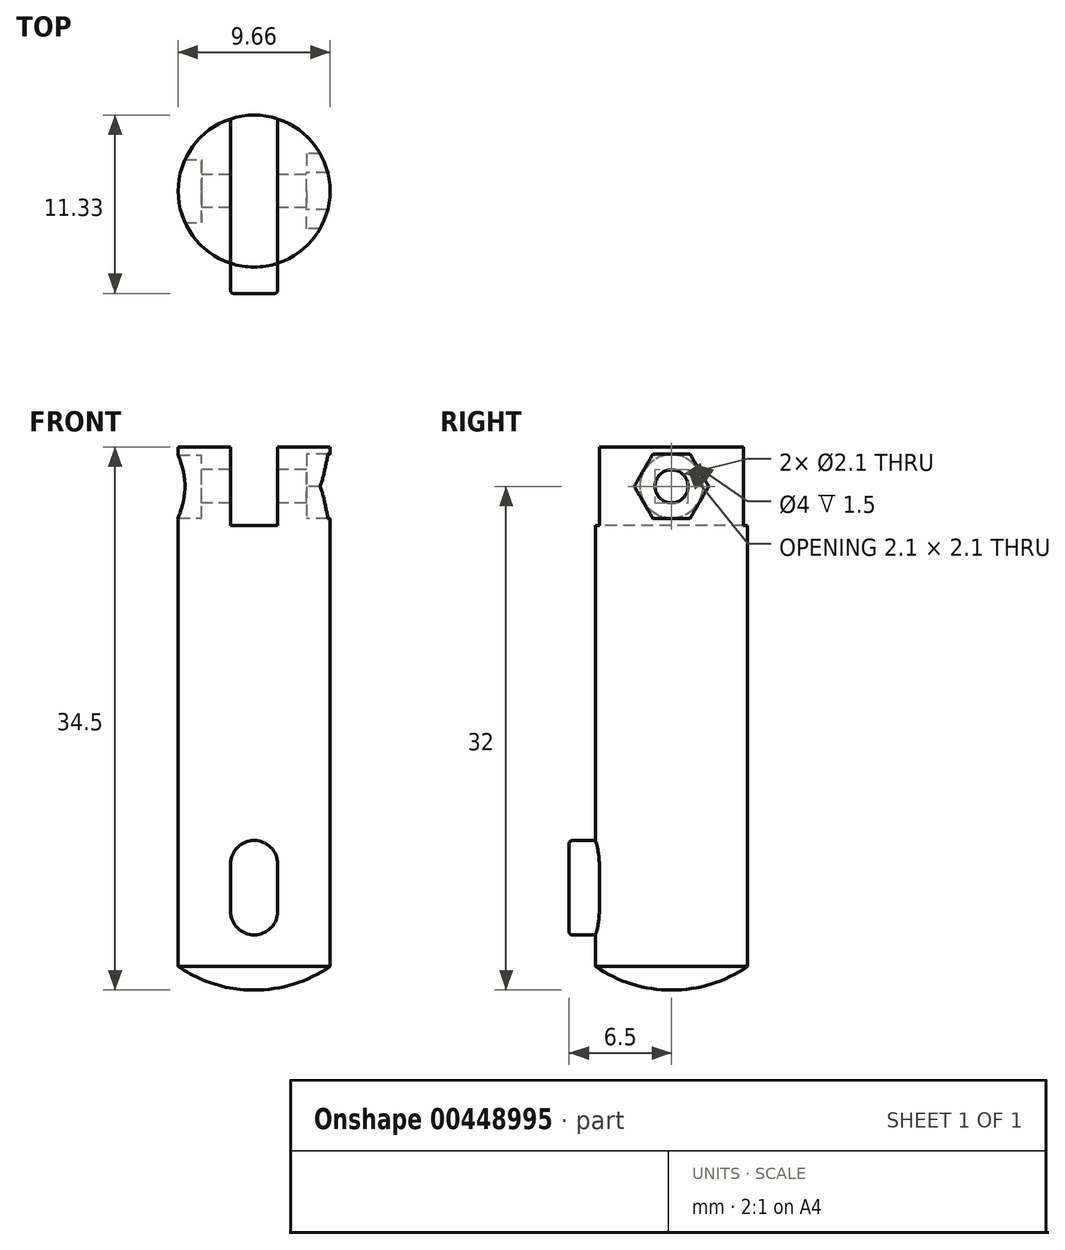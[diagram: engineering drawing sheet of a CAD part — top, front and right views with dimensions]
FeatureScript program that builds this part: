
annotation { "Feature Type Name" : "Feature", "Feature Type Description" : "" }
export const myFeature = defineFeature(function(context is Context, id is Id, definition is map)
    precondition{}
    {
        {
            var Q0;
            Q0=qCreatedBy(makeId("Top.planeOp"),FACE);
            var sketch = newSketch(context, id + "F0", { "sketchPlane" : qUnion([Q0])});
            skCircle(sketch, "E0", {"center": v(0, 0) * mm, "radius": 4.83 * mm});
            skSolve(sketch);
        }
        {
            var Q0;
            Q0 = qSketchRegion(id + "F0", true);
            extrude(context, id + "F1", {"entities" : qUnion([Q0]), "depth" : 33 * mm});
        }
        {
            var Q0;
            Q0=qCreatedBy(makeId("Front.planeOp"),FACE);
            var sketch = newSketch(context, id + "F2", { "sketchPlane" : qUnion([Q0])});
            skLineSegment(sketch, "E1", {"start": v(0, 3.5) * mm, "end": v(0, 6.5) * mm, "construction": true});
            skArc(sketch, "E2.0.startCap", {"start": v(1.5, 3.5) * mm, "mid": v(0, 2) * mm, "end": v(-1.5, 3.5) * mm});
            skArc(sketch, "E2.0.endCap", {"start": v(-1.5, 6.5) * mm, "mid": v(0, 8) * mm, "end": v(1.5, 6.5) * mm});
            skLineSegment(sketch, "E2.0.left", {"start": v(-1.5, 3.5) * mm, "end": v(-1.5, 6.5) * mm});
            skLineSegment(sketch, "E2.0.right", {"start": v(1.5, 3.5) * mm, "end": v(1.5, 6.5) * mm});
            skSolve(sketch);
        }
        {
            var Q0;
            Q0 = qSketchRegion(id + "F2", true);
            var Q1;
            Q1 = qBodyType(qCreatedBy(id + "F2" ,EDGE), BodyType.WIRE);
            extrude(context, id + "F3", {"entities" : qUnion([Q0]), "operationType" : NewBodyOperationType.ADD, "surfaceEntities" : qUnion([Q1]), "depth" : 6.5 * mm});
        }
        {
            var Q0;
            Q0=makeQuery(id+"F3.opExtrude","CAP_FACE",FACE,{"disambiguationData":[OSD([sQuery(id+"F2.wireOp",EDGE,"E2.0.startCap"),sQuery(id+"F2.wireOp",EDGE,"E2.0.endCap"),sQuery(id+"F2.wireOp",EDGE,"E2.0.left"),sQuery(id+"F2.wireOp",EDGE,"E2.0.right")])],"isStart":false});
            fillet(context, id + "F4", {"entities" : qUnion([Q0]), "radius" : 0.2 * mm, "tangentPropagation" : true, "allowEdgeOverflow" : false});
        }
        {
            var Q0;
            Q0=qCreatedBy(makeId("Front.planeOp"),FACE);
            var sketch = newSketch(context, id + "F5", { "sketchPlane" : qUnion([Q0])});
            skLineSegment(sketch, "E3", {"start": v(0, 0) * mm, "end": v(0, -2.82) * mm, "construction": true});
            skLineSegment(sketch, "E4", {"start": v(-4.62, -1.5) * mm, "end": v(4.9, -1.5) * mm, "construction": true});
            skLineSegment(sketch, "E5.0", {"start": v(-4.83, 0) * mm, "end": v(0, 0) * mm});
            skArc(sketch, "E6", {"start": v(-4.83, 0) * mm, "mid": v(-2.53, -1.12) * mm, "end": v(0, -1.5) * mm});
            skLineSegment(sketch, "E7", {"start": v(0, 0) * mm, "end": v(0, -1.5) * mm});
            skPoint(sketch, "E8.orphan", {"position": v(4.83, 0) * mm});
            skSolve(sketch);
        }
        {
            var Q0;
            Q0 = qSketchRegion(id + "F5", true);
            var Q1;
            Q1=sQuery(id+"F5.wireOp",EDGE,"E3");
            revolve(context, id + "F6", {"operationType" : NewBodyOperationType.ADD, "entities" : qUnion([Q0]), "axis" : qUnion([Q1]), "revolveType" : RevolveType.FULL});
        }
        {
            var Q0;
            Q0=makeQuery(id+"F1.opExtrude","CAP_FACE",FACE,{"disambiguationData":[OSD([sQuery(id+"F0.wireOp",EDGE,"E0")])],"isStart":false});
            var sketch = newSketch(context, id + "F7", { "sketchPlane" : qUnion([Q0])});
            skLineSegment(sketch, "E9", {"start": v(0, 11.02) * mm, "end": v(0, -10.17) * mm, "construction": true});
            skLineSegment(sketch, "E10.0", {"start": v(-1.5, 4.59) * mm, "end": v(-1.5, -4.59) * mm});
            skLineSegment(sketch, "E11.0", {"start": v(1.5, 4.59) * mm, "end": v(1.5, -4.59) * mm});
            skArc(sketch, "E12.0", {"start": v(1.5, 4.59) * mm, "mid": v(0, 4.83) * mm, "end": v(-1.5, 4.59) * mm});
            skArc(sketch, "E13.trimOffspring", {"start": v(-1.5, -4.59) * mm, "mid": v(0, -4.83) * mm, "end": v(1.5, -4.59) * mm});
            skSolve(sketch);
        }
        {
            var Q0;
            Q0 = qSketchRegion(id + "F7", true);
            extrude(context, id + "F8", {"entities" : qUnion([Q0]), "operationType" : NewBodyOperationType.REMOVE, "oppositeDirection" : true, "depth" : 5 * mm});
        }
        {
            var Q0;
            Q0=qCreatedBy(makeId("Right.planeOp"),FACE);
            var sketch = newSketch(context, id + "F9", { "sketchPlane" : qUnion([Q0])});
            skCircle(sketch, "E14", {"center": v(0, 30.5) * mm, "radius": 1.05 * mm});
            skSolve(sketch);
        }
        {
            var Q0;
            Q0 = qSketchRegion(id + "F9", true);
            extrude(context, id + "F10", {"entities" : qUnion([Q0]), "operationType" : NewBodyOperationType.REMOVE, "endBound" : BoundingType.THROUGH_ALL, "depth" : 25 * mm, "hasSecondDirection" : true, "secondDirectionBound" : SecondDirectionBoundingType.THROUGH_ALL, "secondDirectionOppositeDirection" : true, "secondDirectionDepth" : 25 * mm});
        }
        {
            var Q0;
            Q0=qCreatedBy(makeId("Right.planeOp"),FACE);
            var sketch = newSketch(context, id + "F11", { "sketchPlane" : qUnion([Q0])});
            skCircle(sketch, "E15.0", {"center": v(0, 30.5) * mm, "radius": 1.05 * mm, "construction": true});
            skCircle(sketch, "E16.cCircle", {"center": v(0, 30.5) * mm, "radius": 2.05 * mm, "construction": true});
            skLineSegment(sketch, "E16.0", {"start": v(2.37, 30.5) * mm, "end": v(1.18, 28.45) * mm});
            skLineSegment(sketch, "E16.1", {"start": v(1.18, 28.45) * mm, "end": v(-1.18, 28.45) * mm});
            skLineSegment(sketch, "E16.2", {"start": v(-1.18, 28.45) * mm, "end": v(-2.37, 30.5) * mm});
            skLineSegment(sketch, "E16.3", {"start": v(-2.37, 30.5) * mm, "end": v(-1.18, 32.55) * mm});
            skLineSegment(sketch, "E16.4", {"start": v(-1.18, 32.55) * mm, "end": v(1.18, 32.55) * mm});
            skLineSegment(sketch, "E16.5", {"start": v(1.18, 32.55) * mm, "end": v(2.37, 30.5) * mm});
            skPoint(sketch, "E16.0.midPoint", {"position": v(1.78, 29.48) * mm});
            skLineSegment(sketch, "E17.0", {"start": v(-4.59, 33) * mm, "end": v(4.59, 33) * mm, "construction": true});
            skSolve(sketch);
        }
        {
            var Q0;
            Q0 = qSketchRegion(id + "F11", true);
            extrude(context, id + "F12", {"entities" : qUnion([Q0]), "operationType" : NewBodyOperationType.REMOVE, "endBound" : BoundingType.THROUGH_ALL, "depth" : 25 * mm, "hasSecondDirection" : true, "secondDirectionOppositeDirection" : false, "secondDirectionDepth" : 3.33 * mm});
        }
        {
            var Q0;
            Q0=qCreatedBy(makeId("Right.planeOp"),FACE);
            var sketch = newSketch(context, id + "F13", { "sketchPlane" : qUnion([Q0])});
            skCircle(sketch, "E18.0", {"center": v(0, 30.5) * mm, "radius": 1.05 * mm, "construction": true});
            skCircle(sketch, "E19", {"center": v(0, 30.5) * mm, "radius": 2 * mm});
            skSolve(sketch);
        }
        {
            var Q0;
            Q0 = qSketchRegion(id + "F13", true);
            extrude(context, id + "F14", {"entities" : qUnion([Q0]), "operationType" : NewBodyOperationType.REMOVE, "endBound" : BoundingType.THROUGH_ALL, "oppositeDirection" : true, "depth" : 25 * mm, "hasSecondDirection" : true, "secondDirectionOppositeDirection" : true, "secondDirectionDepth" : 3.33 * mm});
        }
    });
